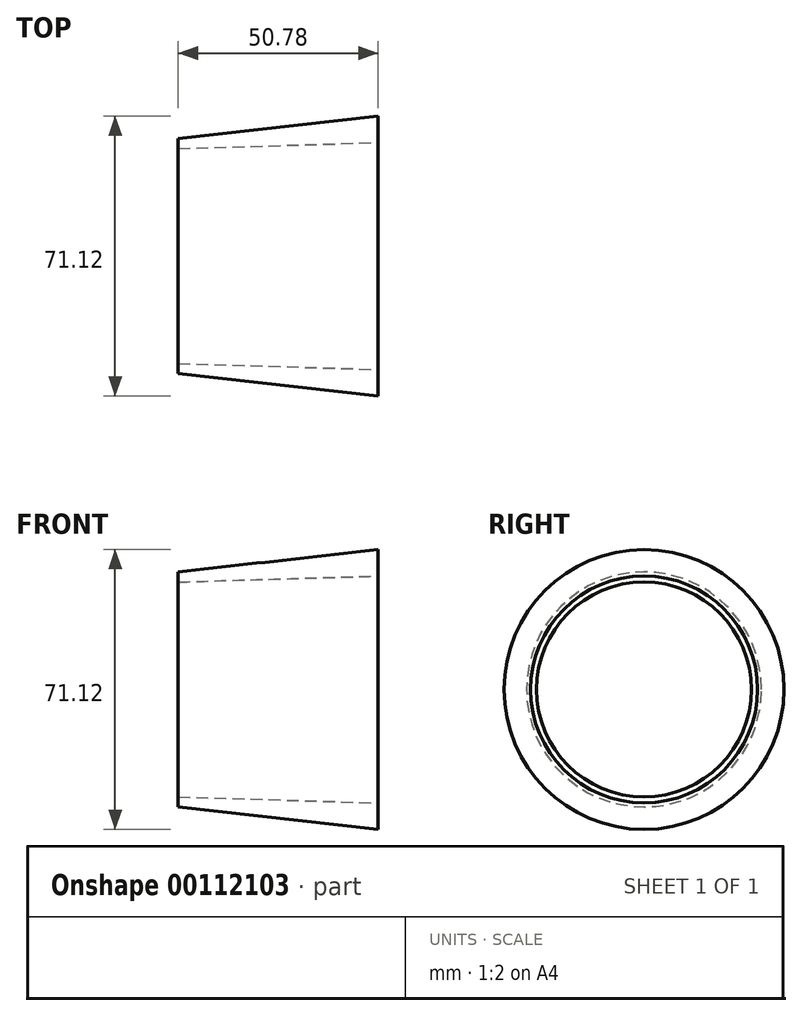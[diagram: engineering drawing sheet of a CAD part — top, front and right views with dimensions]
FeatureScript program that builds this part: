
annotation { "Feature Type Name" : "Feature", "Feature Type Description" : "" }
export const myFeature = defineFeature(function(context is Context, id is Id, definition is map)
    precondition{}
    {
        {
            var Q0;
            Q0=qCreatedBy(makeId("Top.planeOp"),FACE);
            var sketch = newSketch(context, id + "F0", { "sketchPlane" : qUnion([Q0])});
            skLineSegment(sketch, "E0", {"start": v(0, 0) * mm, "end": v(82.28, 0) * mm, "construction": true});
            skLineSegment(sketch, "E1", {"start": v(0, 29.84) * mm, "end": v(50.78, 35.56) * mm});
            skLineSegment(sketch, "E2", {"start": v(50.78, 35.56) * mm, "end": v(50.78, 28.83) * mm});
            skLineSegment(sketch, "E3", {"start": v(50.78, 28.83) * mm, "end": v(0, 27.3) * mm});
            skLineSegment(sketch, "E4", {"start": v(0, 27.3) * mm, "end": v(0, 29.85) * mm});
            skSolve(sketch);
        }
        {
            var Q0;
            Q0=makeQuery(id+"F0.imprint","IMPRINT",FACE,{"disambiguationData":[TD([[makeQuery(id+"F0.imprint","IMPRINT",EDGE,{"derivedFrom":sQuery(id+"F0.wireOp",EDGE,"E1")}),-1.0]])]});
            var Q1;
            Q1=sQuery(id+"F0.wireOp",EDGE,"E0");
            revolve(context, id + "F1", {"entities" : qUnion([Q0]), "axis" : qUnion([Q1]), "revolveType" : RevolveType.FULL});
        }
    });
